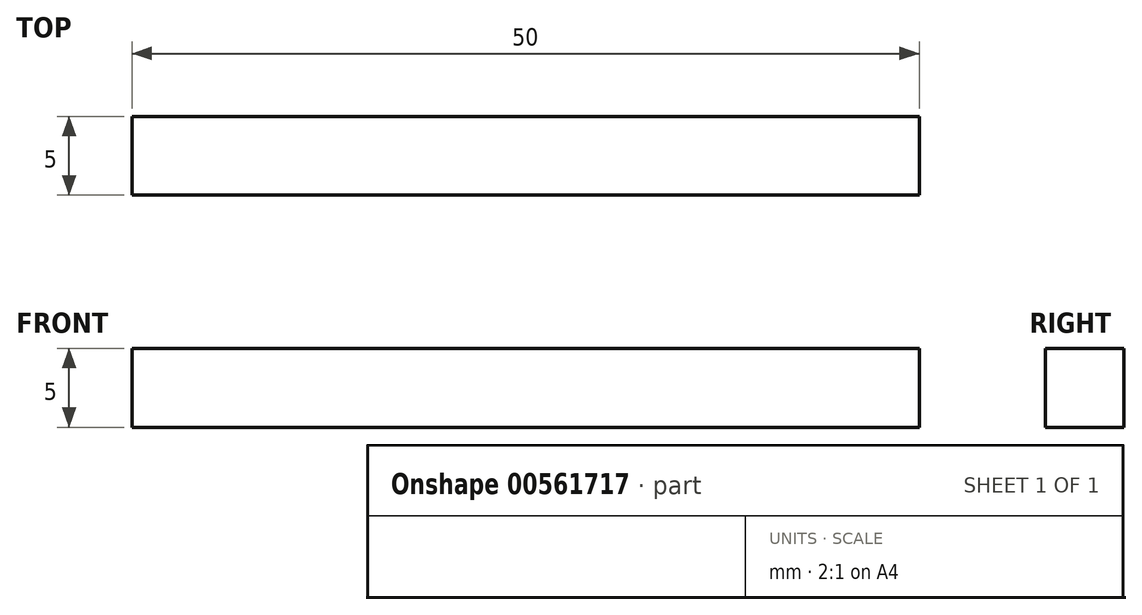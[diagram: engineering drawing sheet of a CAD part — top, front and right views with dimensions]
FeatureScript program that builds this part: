
annotation { "Feature Type Name" : "Feature", "Feature Type Description" : "" }
export const myFeature = defineFeature(function(context is Context, id is Id, definition is map)
    precondition{}
    {
        {
            var Q0;
            Q0=qCreatedBy(makeId("Front.planeOp"),FACE);
            var sketch = newSketch(context, id + "F0", { "sketchPlane" : qUnion([Q0])});
            skLineSegment(sketch, "E0", {"start": v(-11.48, 0) * mm, "end": v(-61.48, 0) * mm});
            skLineSegment(sketch, "E1", {"start": v(-61.48, 0) * mm, "end": v(-61.48, 5) * mm});
            skLineSegment(sketch, "E2", {"start": v(-61.48, 5) * mm, "end": v(-11.48, 5) * mm});
            skLineSegment(sketch, "E3", {"start": v(-11.48, 5) * mm, "end": v(-11.48, 0) * mm});
            skSolve(sketch);
        }
        {
            var Q0;
            Q0=makeQuery(id+"F0.imprint","IMPRINT",FACE,{"disambiguationData":[TD([[makeQuery(id+"F0.imprint","IMPRINT",EDGE,{"derivedFrom":sQuery(id+"F0.wireOp",EDGE,"E0")}),-1.0]])]});
            extrude(context, id + "F1", {"entities" : qUnion([Q0]), "depth" : 5 * mm, "offsetDistance" : 25 * mm});
        }
    });
